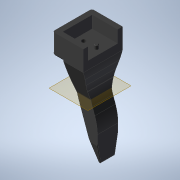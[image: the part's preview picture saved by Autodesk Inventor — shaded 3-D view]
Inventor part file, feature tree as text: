
AUTODESK INVENTOR PART (.ipt)
format: ipt  version: 2020 (Build 240168000, 168)  size: 303,616 bytes
history: native  units: mm
features: sketch x9, extrude x8, chamfer x3, mirror x1, hole x1, plane x1, fillet x1, imported_body x1
ambient origin geometry x8: Origin, YZ Plane, XZ Plane, XY Plane, X Axis, Y Axis, Z Axis, Center Point
bodies: Solid1 (feature_tree)
feature tree (25):
  extrude  "Extrusion1"  Depth=9.5mm TaperAngle=0.0deg
  extrude  "Extrusion2"  Depth=9.5mm TaperAngle=45.0deg
  chamfer  "Chamfer6"  Distance=11.0mm
  mirror  "Mirror2"
  chamfer  "Chamfer7"  Distance=12.5mm
  extrude  "Extrusion7"  Depth=4.0mm
  extrude  "Extrusion8"  Depth=4.0mm
  hole  "Hole2"  [1 undecoded]
  extrude  "Extrusion9"  [1 undecoded]
  extrude  "Extrusion11"  Depth=2.0mm TaperAngle=0.0deg
  extrude  "Extrusion10"  Depth=2.0mm TaperAngle=0.0deg
  plane  "Work Plane1"
  extrude  "Extrusion12"  Depth=2.0mm
  fillet  "Fillet1"  Radius=0.5mm
  chamfer  "Chamfer8"  Distance=0.5mm
  sketch  "Sketch1"  dims[d0=20.0mm d1=0.0mm d4=9.5mm d5=0.0mm]
  sketch  "Sketch3"  dims[d45=9.5mm d46=30.0mm d47=45.0deg d48=9.5mm d49=30.0mm d50=45.0deg d51=11.0mm d52=0.0mm]
  sketch  "Sketch10"  dims[d53=26.0mm]
  sketch  "Sketch11"  dims[d54=30.2mm d55=12.5mm d56=0.0mm]
  sketch  "Sketch12"  dims[d57=4.5mm d58=6.0mm d59=12.24mm d60=3.58mm d61=90.0deg d62=8.0mm d63=20.594885mm d65=4.0mm]
  sketch  "Sketch13"  dims[d66=4.0mm d67=0.0mm d68=13.0mm]
  sketch  "Sketch14"  dims[d69=6.5mm d70=50.0mm d71=0.0mm]
  sketch  "Sketch16"  dims[d72=21.0mm d73=0.0mm d75=-50.0mm]
  sketch  "Sketch19"  dims[d76=7.5mm d77=30.0mm d78=0.0mm d79=15.0mm d80=0.0mm d81=2.0mm d82=0.5mm d83=30.0mm d84=45.0deg d25=0.5mm d26=0.872665mm d27=0.5mm d28=0.872665mm]
  imported_body  "Base1"
note: 2 required parameter values undecoded (feature->parameter linkage not recoverable at this tier; creation-order binding heuristic only, values carry confidence <= 0.55)
